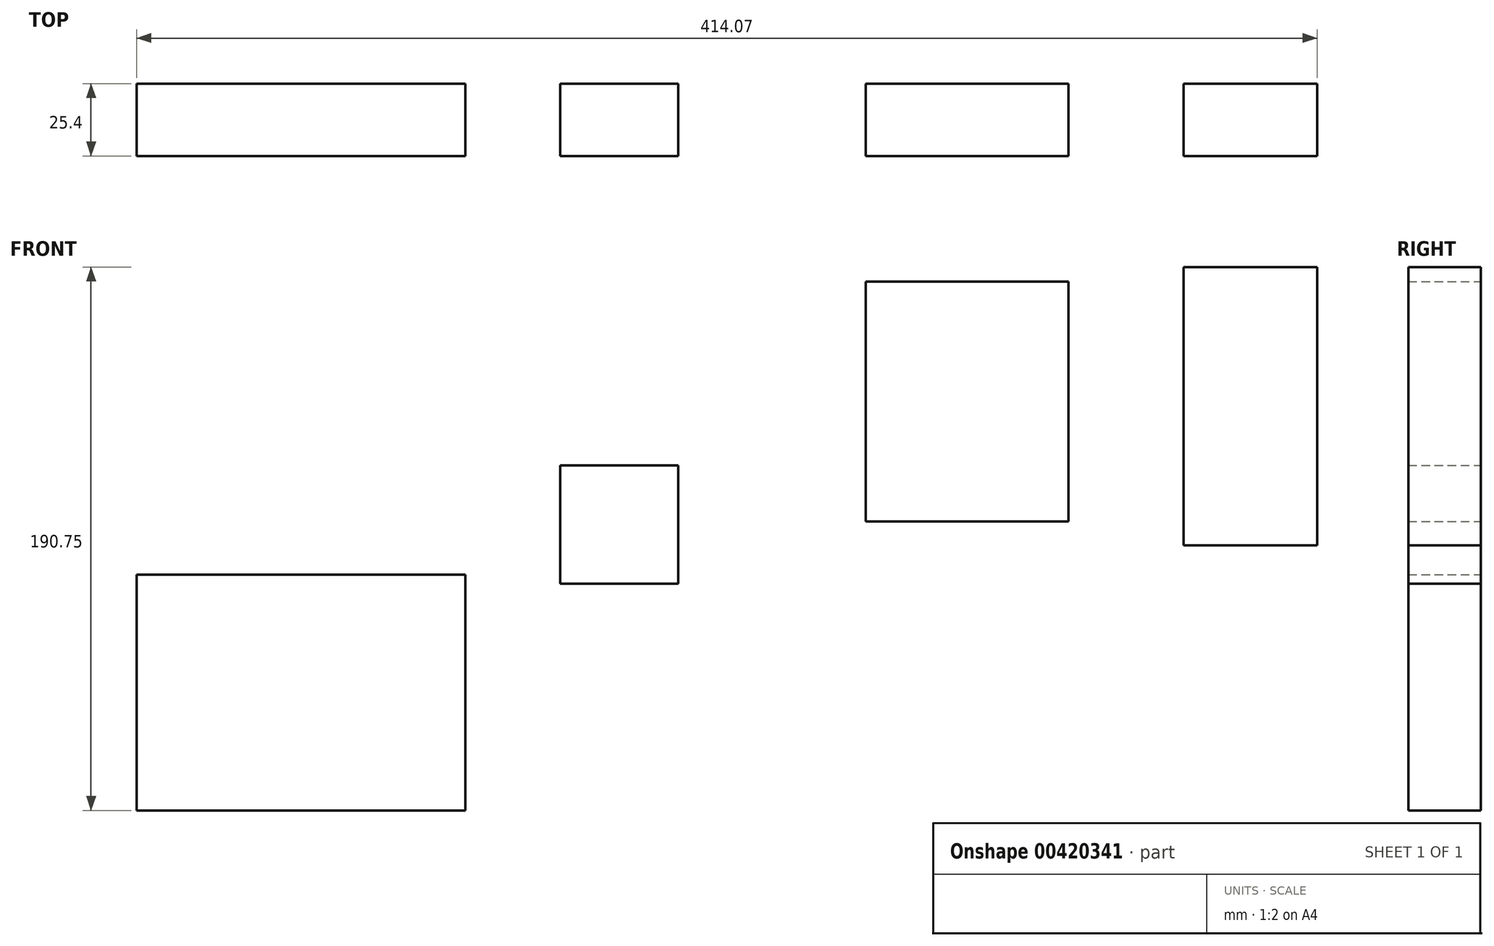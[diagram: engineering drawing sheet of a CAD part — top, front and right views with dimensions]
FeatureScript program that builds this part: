
annotation { "Feature Type Name" : "Feature", "Feature Type Description" : "" }
export const myFeature = defineFeature(function(context is Context, id is Id, definition is map)
    precondition{}
    {
        {
            var Q0;
            Q0=qCreatedBy(makeId("Front.planeOp"),FACE);
            var sketch = newSketch(context, id + "F0", { "sketchPlane" : qUnion([Q0])});
            skLineSegment(sketch, "E0.bottom", {"start": v(-198.05, 6.92) * mm, "end": v(-82.75, 6.92) * mm});
            skLineSegment(sketch, "E0.top", {"start": v(-198.05, -75.77) * mm, "end": v(-82.75, -75.77) * mm});
            skLineSegment(sketch, "E0.left", {"start": v(-198.05, 6.92) * mm, "end": v(-198.05, -75.77) * mm});
            skLineSegment(sketch, "E0.right", {"start": v(-82.75, 6.92) * mm, "end": v(-82.75, -75.77) * mm});
            skLineSegment(sketch, "E1.bottom", {"start": v(-49.51, 45.4) * mm, "end": v(-8.14, 45.4) * mm});
            skLineSegment(sketch, "E1.top", {"start": v(-49.51, 3.75) * mm, "end": v(-8.14, 3.75) * mm});
            skLineSegment(sketch, "E1.left", {"start": v(-49.51, 45.4) * mm, "end": v(-49.51, 3.75) * mm});
            skLineSegment(sketch, "E1.right", {"start": v(-8.14, 45.4) * mm, "end": v(-8.14, 3.75) * mm});
            skLineSegment(sketch, "E2.bottom", {"start": v(57.65, 109.9) * mm, "end": v(128.87, 109.9) * mm});
            skLineSegment(sketch, "E2.top", {"start": v(57.65, 25.67) * mm, "end": v(128.87, 25.67) * mm});
            skLineSegment(sketch, "E2.left", {"start": v(57.65, 109.9) * mm, "end": v(57.65, 25.67) * mm});
            skLineSegment(sketch, "E2.right", {"start": v(128.87, 109.9) * mm, "end": v(128.87, 25.67) * mm});
            skLineSegment(sketch, "E3.bottom", {"start": v(169.22, 114.98) * mm, "end": v(216.02, 114.98) * mm});
            skLineSegment(sketch, "E3.top", {"start": v(169.22, 17.26) * mm, "end": v(216.02, 17.26) * mm});
            skLineSegment(sketch, "E3.left", {"start": v(169.22, 114.98) * mm, "end": v(169.22, 17.26) * mm});
            skLineSegment(sketch, "E3.right", {"start": v(216.02, 114.98) * mm, "end": v(216.02, 17.26) * mm});
            skSolve(sketch);
        }
        {
            var Q0;
            Q0 = qSketchRegion(id + "F0", true);
            extrude(context, id + "F1", {"entities" : qUnion([Q0]), "depth" : 25.4 * mm, "offsetDistance" : 25.4 * mm});
        }
    });
